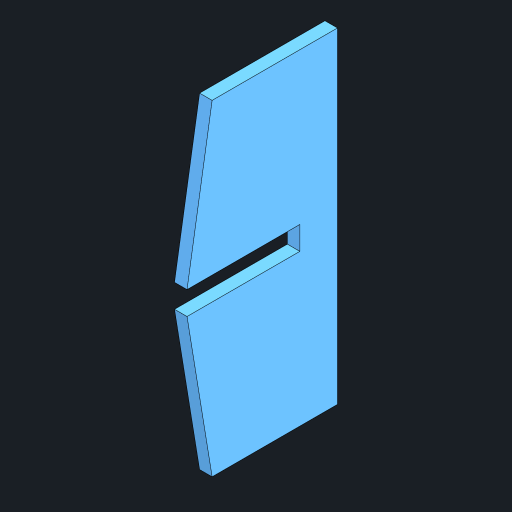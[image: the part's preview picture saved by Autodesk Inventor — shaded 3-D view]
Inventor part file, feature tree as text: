
AUTODESK INVENTOR PART (.ipt)
format: ipt  version: 2023 (Build 270158000, 158)  size: 110,080 bytes
history: native  units: mm
features: other x1, extrude x1, sketch x1
ambient origin geometry x8: Origin, YZ Plane, XZ Plane, XY Plane, X Axis, Y Axis, Z Axis, Center Point
bodies: Body1 (feature_tree)
feature tree (3):
  other  "ソリッド1"
  extrude  "押し出し1"  Depth=4.65mm
  sketch  "スケッチ1"
